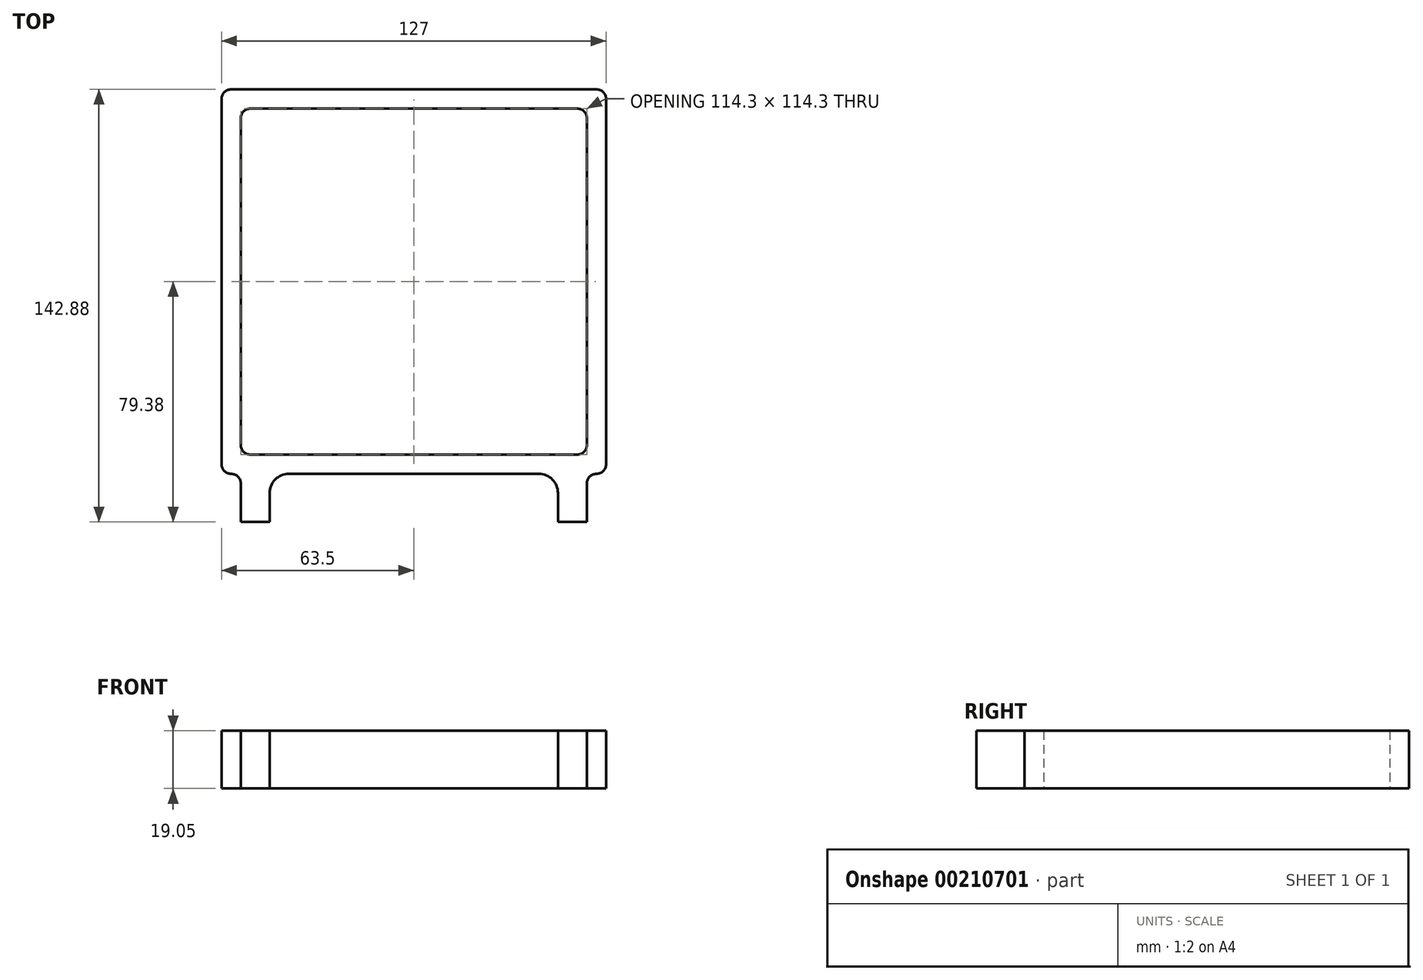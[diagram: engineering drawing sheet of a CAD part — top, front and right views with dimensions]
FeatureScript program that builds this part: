
annotation { "Feature Type Name" : "Feature", "Feature Type Description" : "" }
export const myFeature = defineFeature(function(context is Context, id is Id, definition is map)
    precondition{}
    {
        {
            var Q0;
            Q0=qCreatedBy(makeId("Top.planeOp"),FACE);
            var sketch = newSketch(context, id + "F0", { "sketchPlane" : qUnion([Q0])});
            skLineSegment(sketch, "E0.bottom", {"start": v(-60.33, 63.5) * mm, "end": v(60.33, 63.5) * mm});
            skLineSegment(sketch, "E0.top", {"start": v(-60.33, -63.5) * mm, "end": v(-60.32, -63.5) * mm});
            skLineSegment(sketch, "E0.left", {"start": v(-63.5, 60.32) * mm, "end": v(-63.5, -60.32) * mm});
            skLineSegment(sketch, "E0.right", {"start": v(63.5, 60.33) * mm, "end": v(63.5, -60.32) * mm});
            skPoint(sketch, "E1.visualSharp", {"position": v(-63.5, 63.5) * mm});
            skArc(sketch, "E1.filletArc", {"start": v(-60.33, 63.5) * mm, "mid": v(-62.57, 62.57) * mm, "end": v(-63.5, 60.32) * mm});
            skPoint(sketch, "E2.visualSharp", {"position": v(63.5, 63.5) * mm});
            skArc(sketch, "E2.filletArc", {"start": v(63.5, 60.33) * mm, "mid": v(62.57, 62.57) * mm, "end": v(60.33, 63.5) * mm});
            skPoint(sketch, "E3.visualSharp", {"position": v(63.5, -63.5) * mm});
            skArc(sketch, "E3.filletArc", {"start": v(60.33, -63.5) * mm, "mid": v(62.57, -62.57) * mm, "end": v(63.5, -60.32) * mm});
            skPoint(sketch, "E4.visualSharp", {"position": v(-63.5, -63.5) * mm});
            skArc(sketch, "E4.filletArc", {"start": v(-63.5, -60.32) * mm, "mid": v(-62.57, -62.57) * mm, "end": v(-60.33, -63.5) * mm});
            skLineSegment(sketch, "E5.bottom", {"start": v(-53.98, 57.15) * mm, "end": v(53.97, 57.15) * mm});
            skLineSegment(sketch, "E5.top", {"start": v(-53.97, -57.15) * mm, "end": v(53.98, -57.15) * mm});
            skLineSegment(sketch, "E5.left", {"start": v(-57.15, 53.97) * mm, "end": v(-57.15, -53.98) * mm});
            skLineSegment(sketch, "E5.right", {"start": v(57.15, 53.98) * mm, "end": v(57.15, -53.97) * mm});
            skPoint(sketch, "E6.visualSharp", {"position": v(-57.15, 57.15) * mm});
            skArc(sketch, "E6.filletArc", {"start": v(-53.98, 57.15) * mm, "mid": v(-56.22, 56.22) * mm, "end": v(-57.15, 53.97) * mm});
            skPoint(sketch, "E7.visualSharp", {"position": v(57.15, 57.15) * mm});
            skArc(sketch, "E7.filletArc", {"start": v(57.15, 53.98) * mm, "mid": v(56.22, 56.22) * mm, "end": v(53.97, 57.15) * mm});
            skPoint(sketch, "E8.visualSharp", {"position": v(57.15, -57.15) * mm});
            skArc(sketch, "E8.filletArc", {"start": v(53.98, -57.15) * mm, "mid": v(56.22, -56.22) * mm, "end": v(57.15, -53.97) * mm});
            skPoint(sketch, "E9.visualSharp", {"position": v(-57.15, -57.15) * mm});
            skArc(sketch, "E9.filletArc", {"start": v(-57.15, -53.98) * mm, "mid": v(-56.22, -56.22) * mm, "end": v(-53.97, -57.15) * mm});
            skLineSegment(sketch, "E10.top", {"start": v(-57.15, -79.38) * mm, "end": v(-47.62, -79.38) * mm});
            skLineSegment(sketch, "E10.left", {"start": v(-57.15, -66.68) * mm, "end": v(-57.15, -79.38) * mm});
            skLineSegment(sketch, "E10.right", {"start": v(-47.62, -69.85) * mm, "end": v(-47.62, -79.38) * mm});
            skLineSegment(sketch, "E11.top", {"start": v(47.62, -79.38) * mm, "end": v(57.15, -79.38) * mm});
            skLineSegment(sketch, "E11.left", {"start": v(47.62, -69.85) * mm, "end": v(47.62, -79.37) * mm});
            skLineSegment(sketch, "E11.right", {"start": v(57.15, -66.67) * mm, "end": v(57.15, -79.37) * mm});
            skLineSegment(sketch, "E12.trimOffspring", {"start": v(-41.27, -63.5) * mm, "end": v(41.27, -63.5) * mm});
            skLineSegment(sketch, "E13.trimOffspring", {"start": v(60.33, -63.5) * mm, "end": v(60.33, -63.5) * mm});
            skPoint(sketch, "E14.visualSharp", {"position": v(-47.62, -63.5) * mm});
            skArc(sketch, "E14.filletArc", {"start": v(-41.27, -63.5) * mm, "mid": v(-45.77, -65.36) * mm, "end": v(-47.62, -69.85) * mm});
            skPoint(sketch, "E15.visualSharp", {"position": v(47.62, -63.5) * mm});
            skArc(sketch, "E15.filletArc", {"start": v(47.62, -69.85) * mm, "mid": v(45.77, -65.36) * mm, "end": v(41.27, -63.5) * mm});
            skPoint(sketch, "E16.visualSharp", {"position": v(-57.15, -63.5) * mm});
            skArc(sketch, "E16.filletArc", {"start": v(-57.15, -66.68) * mm, "mid": v(-58.08, -64.43) * mm, "end": v(-60.32, -63.5) * mm});
            skPoint(sketch, "E17.visualSharp", {"position": v(57.15, -63.5) * mm});
            skArc(sketch, "E17.filletArc", {"start": v(60.33, -63.5) * mm, "mid": v(58.08, -64.43) * mm, "end": v(57.15, -66.67) * mm});
            skSolve(sketch);
        }
        {
            var Q0;
            Q0 = qSketchRegion(id + "F0", true);
            extrude(context, id + "F1", {"entities" : qUnion([Q0]), "depth" : 19.05 * mm});
        }
    });
